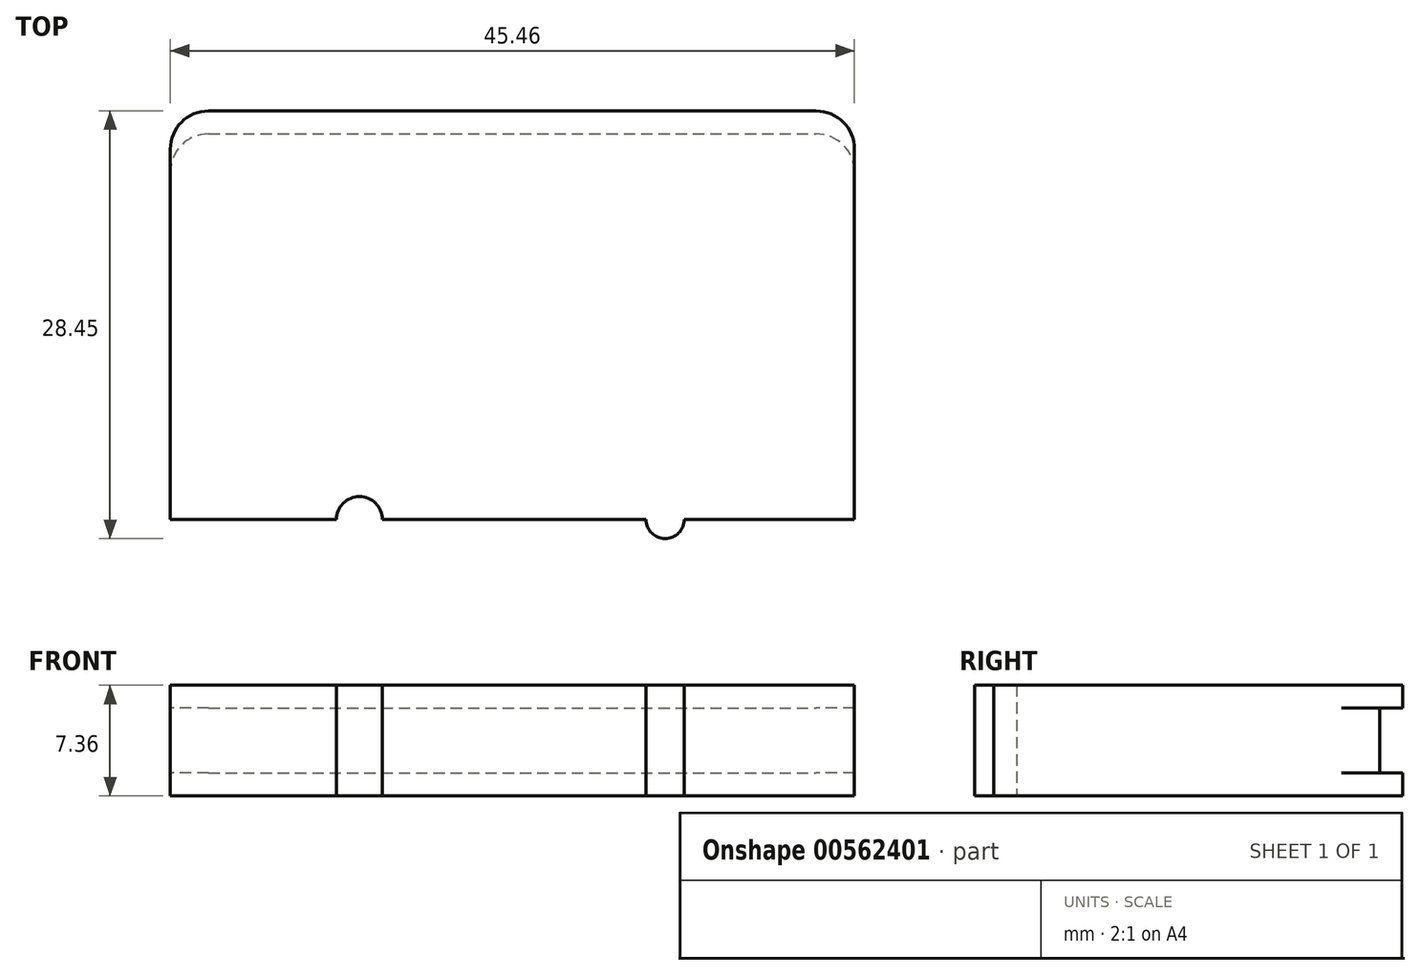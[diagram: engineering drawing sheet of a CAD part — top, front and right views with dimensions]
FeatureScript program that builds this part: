
annotation { "Feature Type Name" : "Feature", "Feature Type Description" : "" }
export const myFeature = defineFeature(function(context is Context, id is Id, definition is map)
    precondition{}
    {
        {
            var Q0;
            Q0=qCreatedBy(makeId("Top.planeOp"),FACE);
            var sketch = newSketch(context, id + "F0", { "sketchPlane" : qUnion([Q0])});
            skLineSegment(sketch, "E0.bottom", {"start": v(-22.73, 0) * mm, "end": v(22.73, 0) * mm});
            skLineSegment(sketch, "E0.top", {"start": v(-20.2, 25.65) * mm, "end": v(20.2, 25.65) * mm});
            skLineSegment(sketch, "E0.left", {"start": v(-22.73, 0) * mm, "end": v(-22.73, 23.11) * mm});
            skLineSegment(sketch, "E0.right", {"start": v(22.73, 0) * mm, "end": v(22.73, 23.11) * mm});
            skPoint(sketch, "E1.visualSharp", {"position": v(-22.73, 25.65) * mm});
            skArc(sketch, "E1.filletArc", {"start": v(-20.2, 25.65) * mm, "mid": v(-21.99, 24.91) * mm, "end": v(-22.73, 23.11) * mm});
            skPoint(sketch, "E2.visualSharp", {"position": v(22.73, 25.65) * mm});
            skArc(sketch, "E2.filletArc", {"start": v(22.73, 23.11) * mm, "mid": v(21.99, 24.91) * mm, "end": v(20.2, 25.65) * mm});
            skLineSegment(sketch, "E3", {"start": v(-22.73, 23.11) * mm, "end": v(-22.73, 24.64) * mm});
            skLineSegment(sketch, "E4", {"start": v(-20.2, 27.18) * mm, "end": v(20.2, 27.18) * mm});
            skLineSegment(sketch, "E5", {"start": v(22.73, 24.64) * mm, "end": v(22.73, 23.11) * mm});
            skPoint(sketch, "E6.visualSharp", {"position": v(-22.73, 27.18) * mm});
            skArc(sketch, "E6.filletArc", {"start": v(-20.2, 27.18) * mm, "mid": v(-21.99, 26.43) * mm, "end": v(-22.73, 24.64) * mm});
            skPoint(sketch, "E7.visualSharp", {"position": v(22.73, 27.18) * mm});
            skArc(sketch, "E7.filletArc", {"start": v(22.73, 24.64) * mm, "mid": v(21.99, 26.43) * mm, "end": v(20.2, 27.18) * mm});
            skArc(sketch, "E8", {"start": v(8.9, 0) * mm, "mid": v(10.16, -1.27) * mm, "end": v(11.43, 0) * mm});
            skArc(sketch, "E9", {"start": v(-11.68, 0) * mm, "mid": v(-10.16, 1.52) * mm, "end": v(-8.64, 0) * mm});
            skSolve(sketch);
        }
        {
            var Q0;
            Q0=makeQuery(id+"F0.imprint","IMPRINT",FACE,{"disambiguationData":[TD([[makeQuery(id+"F0.imprint","IMPRINT",EDGE,{"derivedFrom":sQuery(id+"F0.wireOp",EDGE,"E0.top")}),1.0]])]});
            var Q1;
            Q1=makeQuery(id+"F0.imprint","IMPRINT",FACE,{"disambiguationData":[TD([[makeQuery(id+"F0.imprint","IMPRINT",EDGE,{"derivedFrom":sQuery(id+"F0.wireOp",EDGE,"E0.bottom")}),1.0]])]});
            var Q2;
            {var subQ0=sQuery(id+"F0.wireOp",EDGE,"E8");Q2=makeQuery(id+"F0.imprint","IMPRINT",FACE,{"disambiguationData":[TD([[makeQuery(id+"F0.imprint","IMPRINT",EDGE,{"derivedFrom":subQ0}),1.0]])]});}
            extrude(context, id + "F1", {"entities" : qUnion([Q0, Q1, Q2]), "endBound" : BoundingType.SYMMETRIC, "depth" : 7.37 * mm, "offsetDistance" : 25.4 * mm});
        }
        {
            var Q0;
            Q0=makeQuery(id+"F0.imprint","IMPRINT",FACE,{"disambiguationData":[TD([[makeQuery(id+"F0.imprint","IMPRINT",EDGE,{"derivedFrom":sQuery(id+"F0.wireOp",EDGE,"E0.top")}),1.0]])]});
            extrude(context, id + "F2", {"entities" : qUnion([Q0]), "operationType" : NewBodyOperationType.REMOVE, "endBound" : BoundingType.SYMMETRIC, "oppositeDirection" : true, "depth" : 4.32 * mm, "offsetDistance" : 25.4 * mm});
        }
    });
